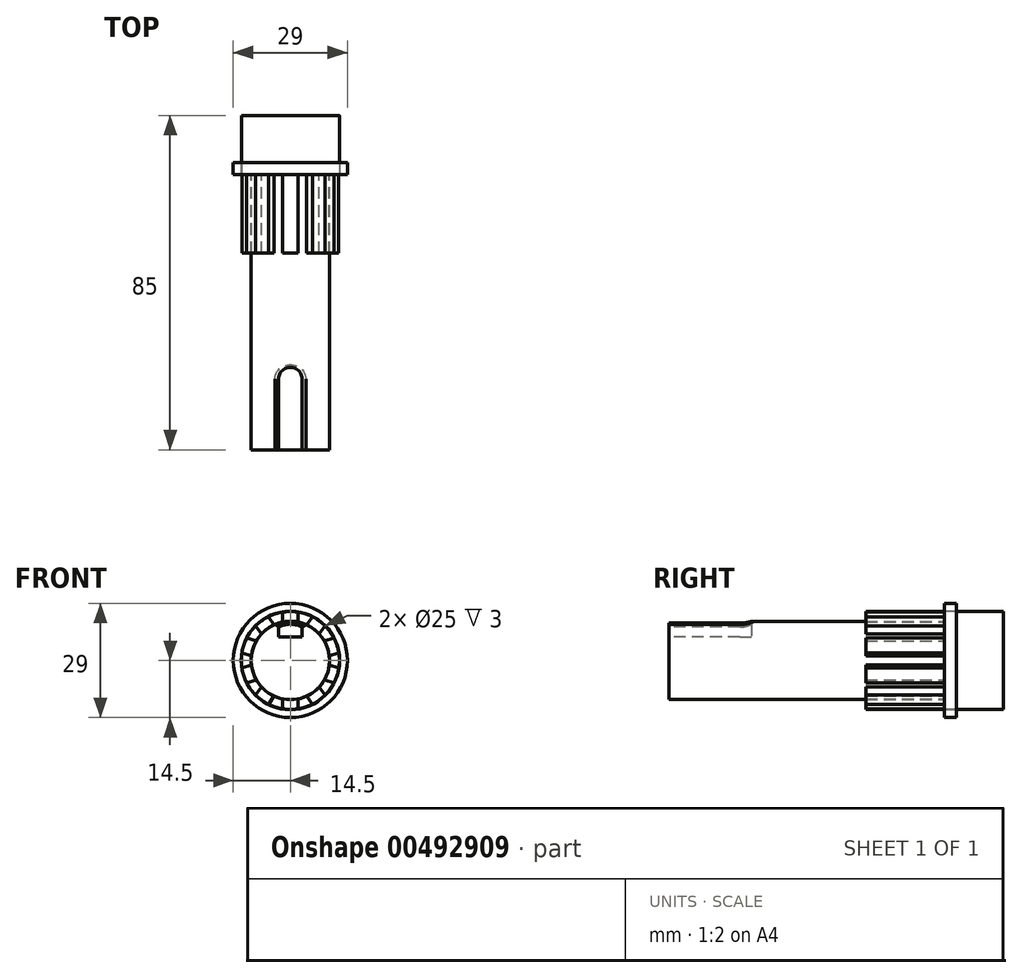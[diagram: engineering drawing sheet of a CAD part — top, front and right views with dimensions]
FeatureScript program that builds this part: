
annotation { "Feature Type Name" : "Feature", "Feature Type Description" : "" }
export const myFeature = defineFeature(function(context is Context, id is Id, definition is map)
    precondition{}
    {
        {
            var Q0;
            Q0=qCreatedBy(makeId("Front.planeOp"),FACE);
            var sketch = newSketch(context, id + "F0", { "sketchPlane" : qUnion([Q0])});
            skCircle(sketch, "E0", {"center": v(0, 0) * mm, "radius": 9.95 * mm});
            skCircle(sketch, "E1", {"center": v(0, 0) * mm, "radius": 12.45 * mm});
            skCircle(sketch, "E2", {"center": v(0, 0) * mm, "radius": 14.5 * mm});
            skCircle(sketch, "E3", {"center": v(0, 0) * mm, "radius": 12.5 * mm});
            skLineSegment(sketch, "E4", {"start": v(-2, 12.34) * mm, "end": v(-2, 9.75) * mm});
            skLineSegment(sketch, "E5", {"start": v(2, 12.34) * mm, "end": v(2, 9.75) * mm});
            skSolve(sketch);
        }
        {
            var Q0;
            Q0=makeQuery(id+"F0.imprint","IMPRINT",FACE,{"disambiguationData":[TD([[makeQuery(id+"F0.imprint","IMPRINT",EDGE,{"derivedFrom":sQuery(id+"F0.wireOp",EDGE,"E0")}),1.0]])]});
            extrude(context, id + "F1", {"entities" : qUnion([Q0]), "depth" : 70 * mm});
        }
        {
            var Q0;
            Q0=makeQuery(id+"F0.imprint","IMPRINT",FACE,{"disambiguationData":[TD([[makeQuery(id+"F0.imprint","IMPRINT",EDGE,{"derivedFrom":sQuery(id+"F0.wireOp",EDGE,"E0")}),1.0]])]});
            extrude(context, id + "F2", {"entities" : qUnion([Q0]), "operationType" : NewBodyOperationType.ADD, "oppositeDirection" : true, "depth" : 15 * mm});
        }
        {
            var Q0;
            Q0=makeQuery(id+"F0.imprint","IMPRINT",FACE,{"disambiguationData":[TD([[makeQuery(id+"F0.imprint","IMPRINT",EDGE,{"derivedFrom":sQuery(id+"F0.wireOp",EDGE,"E0")}),-1.0]])]});
            extrude(context, id + "F3", {"entities" : qUnion([Q0]), "operationType" : NewBodyOperationType.ADD, "oppositeDirection" : true, "depth" : 15 * mm});
        }
        {
            var Q0;
            Q0=makeQuery(id+"F0.imprint","IMPRINT",FACE,{"disambiguationData":[TD([[makeQuery(id+"F0.imprint","IMPRINT",EDGE,{"derivedFrom":sQuery(id+"F0.wireOp",EDGE,"E2")}),1.0]])]});
            extrude(context, id + "F4", {"entities" : qUnion([Q0]), "operationType" : NewBodyOperationType.ADD, "oppositeDirection" : true, "depth" : 3 * mm});
        }
        {
            var Q0;
            Q0=qCreatedBy(makeId("Right.planeOp"),FACE);
            var sketch = newSketch(context, id + "F5", { "sketchPlane" : qUnion([Q0])});
            skLineSegment(sketch, "E6", {"start": v(-72.45, 0) * mm, "end": v(23, 0) * mm, "construction": true});
            skSolve(sketch);
        }
        {
            var Q0;
            Q0=makeQuery(id+"F1.opExtrude","SWEPT_BODY",BODY,{"disambiguationData":[OSD([sQuery(id+"F0.wireOp",EDGE,"E0")])]});
            var Q1;
            Q1=sQuery(id+"F5.wireOp",EDGE,"E6");
            circularPattern(context, id + "F6", {"entities" : qUnion([Q0]), "axis" : qUnion([Q1]), "angle" : 360 * degree, "instanceCount" : 10, "equalSpace" : true, "computeTransformsWithoutBuiltin" : true});
        }
        {
            var Q0;
            Q0=makeQuery(id+"F0.imprint","IMPRINT",FACE,{"disambiguationData":[TD([[makeQuery(id+"F0.imprint","IMPRINT",EDGE,{"derivedFrom":sQuery(id+"F0.wireOp",EDGE,"E2")}),1.0]])]});
            extrude(context, id + "F7", {"entities" : qUnion([Q0]), "oppositeDirection" : true, "depth" : 3 * mm});
        }
        {
            var Q0;
            {var subQ0=sQuery(id+"F0.wireOp",EDGE,"E4");var subQ1=sQuery(id+"F0.wireOp",EDGE,"E0");var subQ2=makeQuery(id+"F0.imprint","INTERSECT",VERTEX,{"derivedFrom":[subQ1,subQ0]});Q0=makeQuery(id+"F0.imprint","IMPRINT",FACE,{"disambiguationData":[TD([[makeQuery(id+"F0.imprint","IMPRINT",EDGE,{"disambiguationData":[TD([[subQ2,1.0]])],"derivedFrom":subQ1}),-1.0]])]});}
            extrude(context, id + "F8", {"entities" : qUnion([Q0]), "depth" : 20 * mm});
        }
        {
            var Q0;
            Q0=qCreatedBy(makeId("Right.planeOp"),FACE);
            var sketch = newSketch(context, id + "F9", { "sketchPlane" : qUnion([Q0])});
            skLineSegment(sketch, "E7", {"start": v(-72.47, 0) * mm, "end": v(21.69, 0) * mm, "construction": true});
            skSolve(sketch);
        }
        {
            var Q0;
            Q0=makeQuery(id+"F8.opExtrude","SWEPT_BODY",BODY,{"disambiguationData":[OSD([sQuery(id+"F0.wireOp",EDGE,"E0"),sQuery(id+"F0.wireOp",EDGE,"E1"),sQuery(id+"F0.wireOp",EDGE,"E4"),sQuery(id+"F0.wireOp",EDGE,"E5")])]});
            var Q1;
            Q1=sQuery(id+"F9.wireOp",EDGE,"E7");
            circularPattern(context, id + "F10", {"entities" : qUnion([Q0]), "axis" : qUnion([Q1]), "angle" : 360 * degree, "instanceCount" : 10, "equalSpace" : true, "computeTransformsWithoutBuiltin" : true});
        }
        {
            var Q0;
            Q0=qCreatedBy(makeId("Top.planeOp"),FACE);
            var Q1;
            Q1 = qBodyType(qCreatedBy(id + "F7BTfUcBMDvFjCz_3" ,EDGE), BodyType.WIRE);
            cPlane(context, id + "F11", {"entities" : qUnion([Q0, Q1]), "cplaneType" : CPlaneType.OFFSET, "offset" : 6 * mm, "width" : 150 * mm, "height" : 150 * mm});
        }
        {
            var Q0;
            Q0=qCreatedBy(id+"F11.planeOp",FACE);
            var sketch = newSketch(context, id + "F12", { "sketchPlane" : qUnion([Q0])});
            skLineSegment(sketch, "E8.top", {"start": v(-3, -77) * mm, "end": v(3, -77) * mm});
            skLineSegment(sketch, "E8.left", {"start": v(-3, -52) * mm, "end": v(-3, -77) * mm});
            skLineSegment(sketch, "E8.right", {"start": v(3, -52) * mm, "end": v(3, -77) * mm});
            skArc(sketch, "E9", {"start": v(3, -52) * mm, "mid": v(0, -49) * mm, "end": v(-3, -52) * mm});
            skSolve(sketch);
        }
        {
            var Q0;
            Q0=makeQuery(id+"F12.imprint","IMPRINT",FACE,{"disambiguationData":[TD([[makeQuery(id+"F12.imprint","IMPRINT",EDGE,{"derivedFrom":sQuery(id+"F12.wireOp",EDGE,"E8.top")}),1.0]])]});
            extrude(context, id + "F13", {"entities" : qUnion([Q0]), "operationType" : NewBodyOperationType.REMOVE, "depth" : 25 * mm, "offsetDistance" : 25 * mm});
        }
        {
            var Q0;
            {var subQ0=sQuery(id+"F0.wireOp",EDGE,"E0");Q0=makeQuery(id+"F13.boolean.opBoolean","INTERSECT",EDGE,{"derivedFrom":[makeQuery(id+"F6.opPattern","COPY",FACE,{"derivedFrom":makeQuery(id+"F2.boolean.opBoolean","MERGE",FACE,{"derivedFrom":[makeQuery(id+"F1.opExtrude","SWEPT_FACE",FACE,{"disambiguationData":[OSD([subQ0])]}),makeQuery(id+"F2.opExtrude","SWEPT_FACE",FACE,{"disambiguationData":[OSD([subQ0])]})]}),"instanceName":"2"}),makeQuery(id+"F13.opExtrude","SWEPT_FACE",FACE,{"disambiguationData":[OSD([sQuery(id+"F12.wireOp",EDGE,"E8.left")])]})]});}
            var Q1;
            {var subQ0=sQuery(id+"F0.wireOp",EDGE,"E0");Q1=makeQuery(id+"F13.boolean.opBoolean","INTERSECT",EDGE,{"derivedFrom":[makeQuery(id+"F6.opPattern","COPY",FACE,{"derivedFrom":makeQuery(id+"F2.boolean.opBoolean","MERGE",FACE,{"derivedFrom":[makeQuery(id+"F1.opExtrude","SWEPT_FACE",FACE,{"disambiguationData":[OSD([subQ0])]}),makeQuery(id+"F2.opExtrude","SWEPT_FACE",FACE,{"disambiguationData":[OSD([subQ0])]})]}),"instanceName":"2"}),makeQuery(id+"F13.opExtrude","SWEPT_FACE",FACE,{"disambiguationData":[OSD([sQuery(id+"F12.wireOp",EDGE,"E9")])]})]});}
            var Q2;
            {var subQ0=sQuery(id+"F0.wireOp",EDGE,"E0");Q2=makeQuery(id+"F13.boolean.opBoolean","INTERSECT",EDGE,{"derivedFrom":[makeQuery(id+"F6.opPattern","COPY",FACE,{"derivedFrom":makeQuery(id+"F2.boolean.opBoolean","MERGE",FACE,{"derivedFrom":[makeQuery(id+"F1.opExtrude","SWEPT_FACE",FACE,{"disambiguationData":[OSD([subQ0])]}),makeQuery(id+"F2.opExtrude","SWEPT_FACE",FACE,{"disambiguationData":[OSD([subQ0])]})]}),"instanceName":"2"}),makeQuery(id+"F13.opExtrude","SWEPT_FACE",FACE,{"disambiguationData":[OSD([sQuery(id+"F12.wireOp",EDGE,"E8.right")])]})]});}
            chamfer(context, id + "F14", {"entities" : qUnion([Q0, Q1, Q2]), "width" : 1 * mm});
        }
    });
